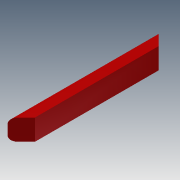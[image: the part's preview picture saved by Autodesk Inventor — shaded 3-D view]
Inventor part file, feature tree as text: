
AUTODESK INVENTOR PART (.ipt)
format: ipt  version: 2014 (Build 180170000, 170)  size: 92,160 bytes
history: native  units: in
note: dims shown in document units (in); Inventor stores cm internally (conversion verified against a paired STEP export)
features: extrude x2, sketch x2
ambient origin geometry x8: Origin, YZ Plane, XZ Plane, XY Plane, X Axis, Y Axis, Z Axis, Center Point
bodies: Solid1 (feature_tree)
feature tree (4):
  extrude  "Extrusion1"  Depth=5.0in
  extrude  "Extrusion2"  Depth=5.0in
  sketch  "Sketch1"  dims[d0=0.75in d1=5.0in]
  sketch  "Sketch2"  dims[d2=2.5in d3=2.5in d4=1.25in d5=36.0in d6=0.0in d8=45.0deg d10=45.0deg d11=5.0in d12=0.0in]
